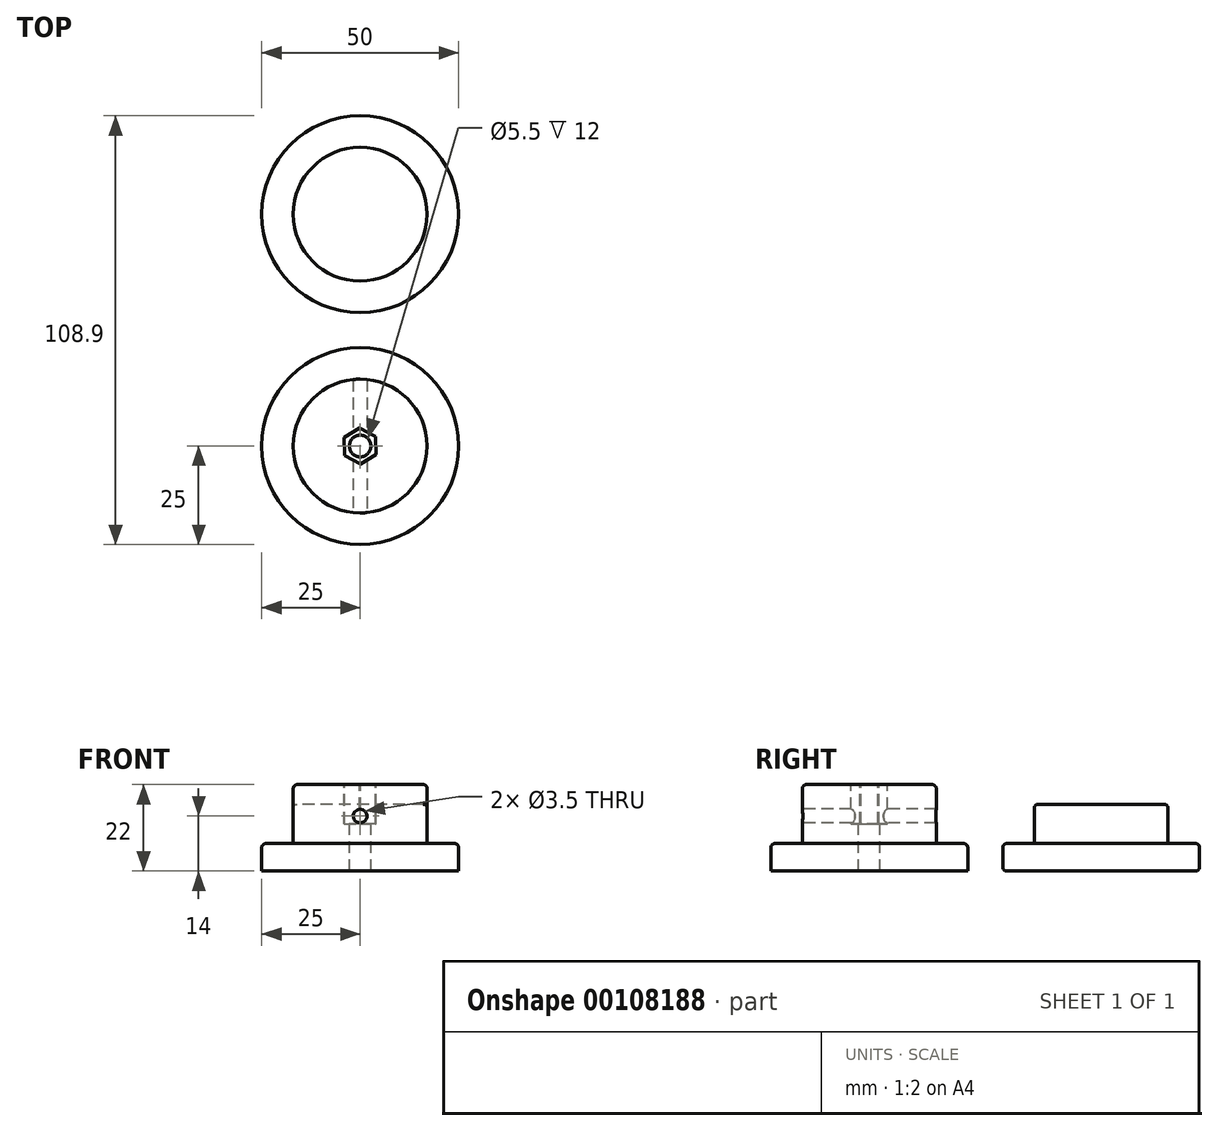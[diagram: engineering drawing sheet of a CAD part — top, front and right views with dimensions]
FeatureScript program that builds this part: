
annotation { "Feature Type Name" : "Feature", "Feature Type Description" : "" }
export const myFeature = defineFeature(function(context is Context, id is Id, definition is map)
    precondition{}
    {
        {
            var Q0;
            Q0=qCreatedBy(makeId("Top.planeOp"),FACE);
            var sketch = newSketch(context, id + "F0", { "sketchPlane" : qUnion([Q0])});
            skCircle(sketch, "E0", {"center": v(0, 0) * mm, "radius": 25 * mm});
            skSolve(sketch);
        }
        {
            var Q0;
            Q0=qCreatedBy(makeId("Top.planeOp"),FACE);
            var sketch = newSketch(context, id + "F1", { "sketchPlane" : qUnion([Q0])});
            skCircle(sketch, "E1", {"center": v(0, 58.9) * mm, "radius": 25 * mm});
            skSolve(sketch);
        }
        {
            var Q0;
            Q0=makeQuery(id+"F0.imprint","IMPRINT",FACE,{"disambiguationData":[TD([[makeQuery(id+"F0.imprint","IMPRINT",EDGE,{"derivedFrom":sQuery(id+"F0.wireOp",EDGE,"E0")}),1.0]])]});
            var Q1;
            Q1 = qSketchRegion(id + "F1", true);
            extrude(context, id + "F2", {"entities" : qUnion([Q0, Q1]), "depth" : 7 * mm});
        }
        {
            var Q0;
            Q0=makeQuery(id+"F2.opExtrude","CAP_FACE",FACE,{"disambiguationData":[OSD([sQuery(id+"F0.wireOp",EDGE,"E0")])],"isStart":false});
            var sketch = newSketch(context, id + "F3", { "sketchPlane" : qUnion([Q0])});
            skCircle(sketch, "E2", {"center": v(0, 0) * mm, "radius": 17 * mm});
            skSolve(sketch);
        }
        {
            var Q0;
            Q0 = qSketchRegion(id + "F3", true);
            extrude(context, id + "F4", {"entities" : qUnion([Q0]), "operationType" : NewBodyOperationType.ADD, "depth" : 15 * mm});
        }
        {
            var Q0;
            Q0=makeQuery(id+"F4.opExtrude","CAP_FACE",FACE,{"disambiguationData":[OSD([sQuery(id+"F3.wireOp",EDGE,"E2")])],"isStart":false});
            var sketch = newSketch(context, id + "F5", { "sketchPlane" : qUnion([Q0])});
            skCircle(sketch, "E3.cCircle", {"center": v(0, 0) * mm, "radius": 4 * mm, "construction": true});
            skLineSegment(sketch, "E3.0", {"start": v(-4.06, 2.2) * mm, "end": v(-0.13, 4.62) * mm});
            skLineSegment(sketch, "E3.1", {"start": v(-0.13, 4.62) * mm, "end": v(3.93, 2.42) * mm});
            skLineSegment(sketch, "E3.2", {"start": v(3.93, 2.42) * mm, "end": v(4.06, -2.2) * mm});
            skLineSegment(sketch, "E3.3", {"start": v(4.06, -2.2) * mm, "end": v(0.13, -4.62) * mm});
            skLineSegment(sketch, "E3.4", {"start": v(0.13, -4.62) * mm, "end": v(-3.93, -2.42) * mm});
            skLineSegment(sketch, "E3.5", {"start": v(-3.93, -2.42) * mm, "end": v(-4.06, 2.2) * mm});
            skPoint(sketch, "E3.0.midPoint", {"position": v(-2.1, 3.4) * mm});
            skSolve(sketch);
        }
        {
            var Q0;
            Q0=makeQuery(id+"F5.imprint","IMPRINT",FACE,{"disambiguationData":[TD([[makeQuery(id+"F5.imprint","IMPRINT",EDGE,{"derivedFrom":sQuery(id+"F5.wireOp",EDGE,"E3.0")}),-1.0]])]});
            extrude(context, id + "F6", {"entities" : qUnion([Q0]), "operationType" : NewBodyOperationType.REMOVE, "oppositeDirection" : true, "depth" : 10 * mm});
        }
        {
            var Q0;
            Q0=makeQuery(id+"F6.boolean.opBoolean","COPY",FACE,{"derivedFrom":makeQuery(id+"F6.opExtrude","CAP_FACE",FACE,{"disambiguationData":[OSD([sQuery(id+"F5.wireOp",EDGE,"E3.0"),sQuery(id+"F5.wireOp",EDGE,"E3.1"),sQuery(id+"F5.wireOp",EDGE,"E3.2"),sQuery(id+"F5.wireOp",EDGE,"E3.3"),sQuery(id+"F5.wireOp",EDGE,"E3.4"),sQuery(id+"F5.wireOp",EDGE,"E3.5")])],"isStart":false})});
            var sketch = newSketch(context, id + "F7", { "sketchPlane" : qUnion([Q0])});
            skCircle(sketch, "E4", {"center": v(0, 0) * mm, "radius": 2.75 * mm});
            skSolve(sketch);
        }
        {
            var Q0;
            Q0=makeQuery(id+"F7.imprint","IMPRINT",FACE,{"disambiguationData":[TD([[makeQuery(id+"F7.imprint","IMPRINT",EDGE,{"derivedFrom":sQuery(id+"F7.wireOp",EDGE,"E4")}),1.0]])]});
            extrude(context, id + "F8", {"entities" : qUnion([Q0]), "operationType" : NewBodyOperationType.REMOVE, "oppositeDirection" : true, "depth" : 25 * mm});
        }
        {
            var Q0;
            Q0=makeQuery(id+"F2.opExtrude","CAP_EDGE",EDGE,{"disambiguationData":[OSD([sQuery(id+"F0.wireOp",EDGE,"E0")])],"isStart":false});
            var Q1;
            Q1=makeQuery(id+"F4.opExtrude","CAP_EDGE",EDGE,{"disambiguationData":[OSD([sQuery(id+"F3.wireOp",EDGE,"E2")])],"isStart":false});
            fillet(context, id + "F9", {"entities" : qUnion([Q0, Q1]), "radius" : 1 * mm, "tangentPropagation" : true, "allowEdgeOverflow" : false});
        }
        {
            var Q0;
            Q0=qCreatedBy(makeId("Front.planeOp"),FACE);
            var sketch = newSketch(context, id + "F10", { "sketchPlane" : qUnion([Q0])});
            skCircle(sketch, "E5", {"center": v(0, 14) * mm, "radius": 1.75 * mm});
            skSolve(sketch);
        }
        {
            var Q0;
            Q0 = qSketchRegion(id + "F10", true);
            var Q1;
            Q1=sQuery(id+"F10.wireOp",EDGE,"E5");
            extrude(context, id + "F11", {"entities" : qUnion([Q0]), "operationType" : NewBodyOperationType.REMOVE, "surfaceEntities" : qUnion([Q1]), "oppositeDirection" : true, "depth" : 25 * mm, "hasSecondDirection" : true, "secondDirectionOppositeDirection" : false, "secondDirectionDepth" : 25 * mm});
        }
        {
            var Q0;
            Q0=makeQuery(id+"F2.opExtrude","CAP_FACE",FACE,{"disambiguationData":[OSD([sQuery(id+"F1.wireOp",EDGE,"E1")])],"isStart":false});
            var sketch = newSketch(context, id + "F12", { "sketchPlane" : qUnion([Q0])});
            skCircle(sketch, "E6", {"center": v(0, 58.9) * mm, "radius": 17 * mm});
            skSolve(sketch);
        }
        {
            var Q0;
            Q0=makeQuery(id+"F12.imprint","IMPRINT",FACE,{"disambiguationData":[TD([[makeQuery(id+"F12.imprint","IMPRINT",EDGE,{"derivedFrom":sQuery(id+"F12.wireOp",EDGE,"E6")}),1.0]])]});
            extrude(context, id + "F13", {"entities" : qUnion([Q0]), "operationType" : NewBodyOperationType.ADD, "depth" : 10 * mm});
        }
        {
            var Q0;
            Q0=makeQuery(id+"F13.opExtrude","CAP_EDGE",EDGE,{"disambiguationData":[OSD([sQuery(id+"F12.wireOp",EDGE,"E6")])],"isStart":false});
            var Q1;
            Q1=makeQuery(id+"F2.opExtrude","CAP_EDGE",EDGE,{"disambiguationData":[OSD([sQuery(id+"F1.wireOp",EDGE,"E1")])],"isStart":false});
            var Q2;
            Q2=makeQuery(id+"F2.opExtrude","CAP_EDGE",EDGE,{"disambiguationData":[OSD([sQuery(id+"F1.wireOp",EDGE,"E1")])],"isStart":true});
            fillet(context, id + "F14", {"entities" : qUnion([Q0, Q1, Q2]), "radius" : 1 * mm, "tangentPropagation" : true, "allowEdgeOverflow" : false});
        }
    });
